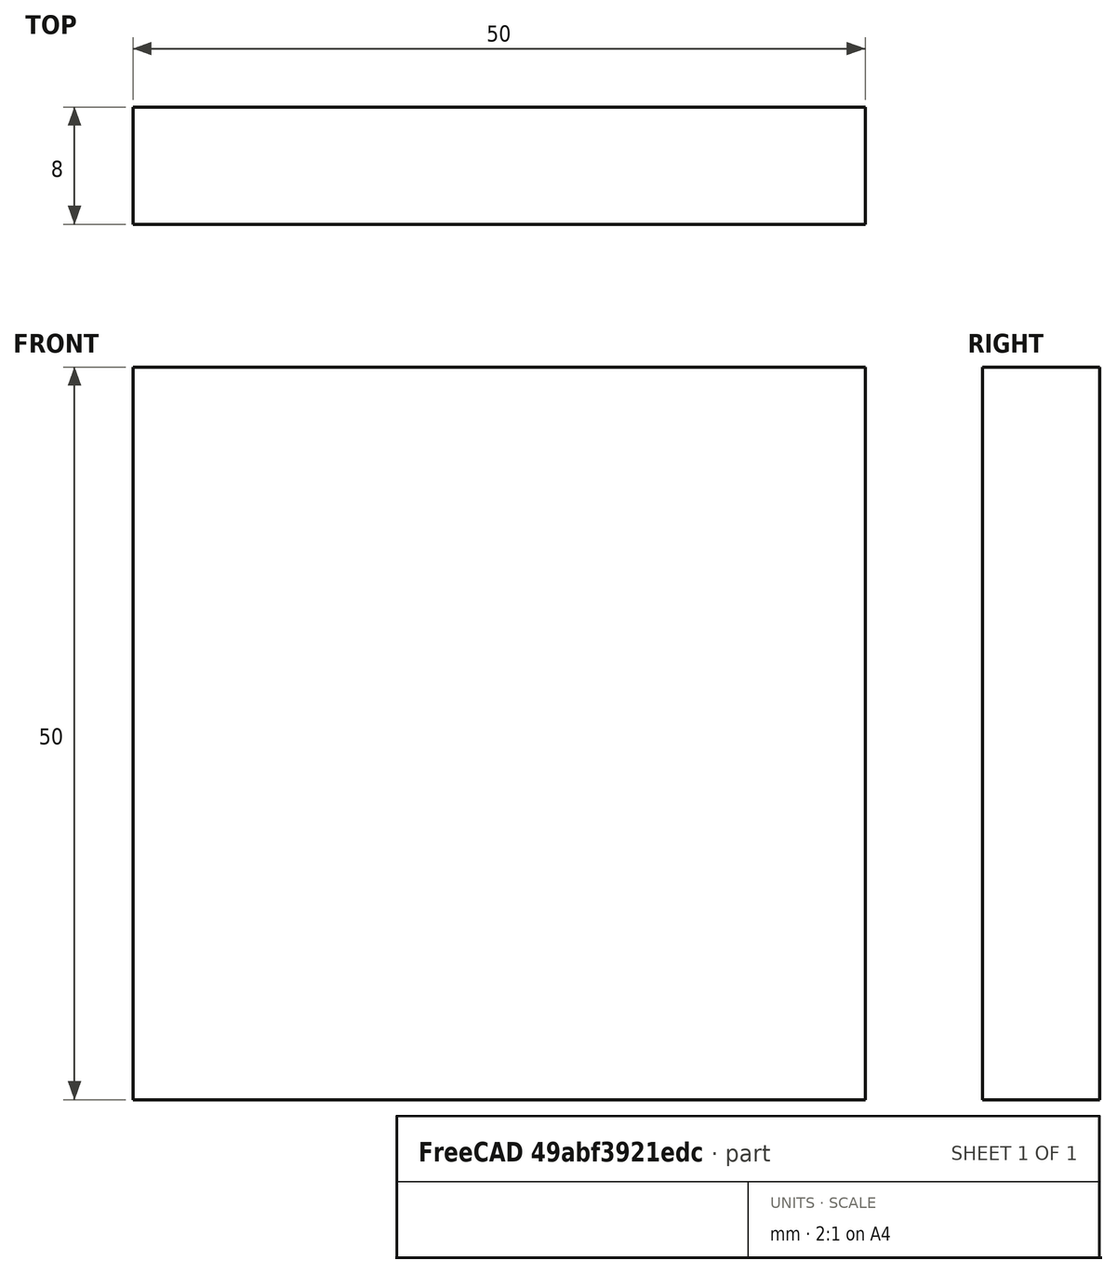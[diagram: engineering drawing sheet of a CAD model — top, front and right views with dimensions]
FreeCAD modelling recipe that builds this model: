
FCSTD DOCUMENT  (FreeCAD 0.15R4671 (Git))
Label: Flat Bar 50x8 EN10058 S235JR
License: All rights reserved
LicenseURL: http://en.wikipedia.org/wiki/All_rights_reserved
objects: Sketcher::SketchObject×1, Part::Extrusion×1
note: 2 computed .brp shape members not serialized (recipe doc carries the construction recipe); baked Part::Feature solids carry a one-line shape summary decoded from their .brp

FEATURE [Sketcher::SketchObject] Sketch
  sketch-geometry (4):
    g0: LineSegment StartX=-25 StartY=-4 StartZ=0 EndX=25 EndY=-4 EndZ=0
    g1: LineSegment StartX=25 StartY=-4 StartZ=0 EndX=25 EndY=4 EndZ=0
    g2: LineSegment StartX=25 StartY=4 StartZ=0 EndX=-25 EndY=4 EndZ=0
    g3: LineSegment StartX=-25 StartY=4 StartZ=0 EndX=-25 EndY=-4 EndZ=0
  constraints (12):
    c: Coincident(g0,g1)
    c: Coincident(g1,g2)
    c: Coincident(g2,g3)
    c: Coincident(g3,g0)
    c: Horizontal(g0)
    c: Horizontal(g2)
    c: Vertical(g1)
    c: Vertical(g3)
    c: Symmetric(g1,g2,g-2)
    c: Symmetric(g0,g1,g-1)
    c: DistanceY(g1) = 8
    c: DistanceX(g0) = 50
FEATURE [Part::Extrusion] Extrude  label="Flat Bar 50x8 EN10058 S235JR"
  Base = -> Sketch
  Dir = (0,0,50)
  Solid = true
